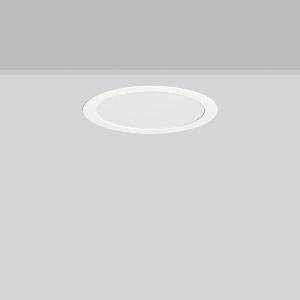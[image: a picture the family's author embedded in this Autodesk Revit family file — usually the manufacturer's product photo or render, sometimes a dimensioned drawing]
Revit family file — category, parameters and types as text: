
# Revit family: toledo_flat__round_e_901808_002_76_de23
name_source: partatom
category: Lighting Fixtures
units: mm (PartAtom-declared; Revit-internal decimal feet)

## family parameters
Cut with Voids When Loaded = No
Host = Face
Light Source = No
Part Type = Normal
Room Calculation Point = No
Round Connector Dimension = Use Diameter
Shared = No

## types (1)
- MultiLumen 1 (1 x LED Modul 840, 1650 lm, 4000)
    Apparent Load = 12 VA
    CIE Flux Codes = 47 79 96 100 100
    Color Rendering = 80
    Color Temperature = 4000
    Default Elevation = 1800 mm
    Description = Series: TOLEDO FLAT+ round
Flexible round recessed multifunction downlight. Housing: sheet steel, powder-coated. Luminaire frame: aluminium, powder-coated. Light guide and diffuser made of non-yellowing PMMA, opal matt. LED backlight technology for homogeneous illumination of the entire light-emitting surface. MultiColour: Colour temperature individually adjustable either 3000 K or 4000 K via switching element. Factory setting is 4000 K. MultiLumen: 4 steps adjustable luminous flux. Factory setting is step 2. Suitable for Recessed ceiling mounting. Ceiling installation with spring system. Can be directly covered with thermal insulation material (applies only to the lower lumen levels). Including separate LED converter with connecting cable 250 mm. Suitable for through wiring as standard. Surface mounted housing as accessory for all sizes. 
Colour: white
Diameter: 270 mm
Height: 2 mm
Cut-out diameter: 257 mm
Recess height: 60 mm
Luminaire: recess height: 40 mm
Lamp: LED
Socket: without socket
Colour temperature: 3000K, 4000K
Colour rendering index (CRI): 80
System power: 12 W
Rated luminous flux: 1650 lm
Luminous efficiency: 138 lm/W
System power 2: 15 W
Rated luminous flux 2: 2200 lm
Luminous efficiency 2: 147 lm/W
System power 3: 19 W
Rated luminous flux 3: 2700 lm
Luminous efficiency 3: 142 lm/W
System power 4: 22 W
Rated luminous flux 4: 3150 lm
Luminous efficiency 4: 143 lm/W
Control gear: Converter, dimmable, DALI
Protection class: II
Type of protection: IP 54
    Height = 0 mm  [stored 0 ft]
    Lamp = 1 x LED Modul 840
    Lamp Light Flux = 1650 lm
    Lamp count = 1
    Length = 270 mm
    Lifetime = 50000 h
    Luminous efficacy = 138 lm/W
    Manufacturer = RZB
    ModVariant = No
    Model = 901808.002.76
    Mounting Place = Ceiling
    Mounting Type = Recessed
    Number of Poles = 1
    OnlyDefault = Yes
    Power Factor = 1
    Product Name = TOLEDO FLAT+ round E
    Product group = Recessed downlights
    ProductGroupID = 402
    Protection Class = Protection class II
    Protection Degree = Degree of protection
    RLX_Detail_Level = 1
    RLX_Emergency_Light_Flux = 0 lm
    RLX_Emergency_Type = 0
    RLX_Emergency_Type_DB = No
    RlxData = <blob elided: 31121 chars, md5=c42a05cb>
    Socket = socket
    Standby Power = 0 W
    System Light Flux = 1650 lm
    System Power = 12 W
    Type Comments = MultiLumen 1
    Type Image = 901808.002.jpg
    URL = http://relux.com
    VarID = multilumen_1
    Voltage = 0 V
    Weight = 0.00 kg
    Width = 0 mm  [stored 0 ft]

note: [stored X ft] marks values corroborated as IEEE doubles in the binary element streams (Revit-internal decimal feet)

## geometry (parser evidence)
native form markers: Blend x4, Sweep x10
no freeform markers — native parametric forms only
